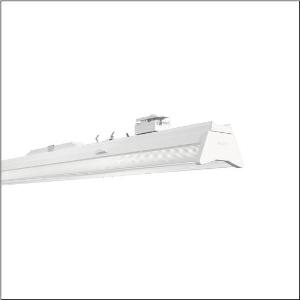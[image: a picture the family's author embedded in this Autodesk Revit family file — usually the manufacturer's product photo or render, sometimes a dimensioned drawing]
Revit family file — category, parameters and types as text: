
# Revit family: licross_r__21_performance_mo_51td16vn445g_3318
name_source: partatom
category: Lighting Fixtures
units: mm (PartAtom-declared; Revit-internal decimal feet)

## family parameters
Cut with Voids When Loaded = No
Host = Face
Light Source = No
Part Type = Normal
Room Calculation Point = No
Round Connector Dimension = Use Diameter
Shared = No

## types (1)
- --- (1 x LED, 4500 lm, 24.2 W, 4000K)
    Apparent Load = 24 VA
    CIE Flux Codes = 66 88 96 79 100
    Color Rendering = 80
    Color Temperature = 4000K
    Default Elevation = 1800 mm
    Description = Licross® 21 Performance MO, luminaire insert, of sheet steel, galvanised, coil coated, white, length: 1.500mm, width: 120mm, height: 123mm, LED rated luminous flux: 4.500lm, light colour: 840, SDCM (Standard Deviation of Colour Matching)MacAdam ≤ 2 SDCM (initial), control gear: DALI 2, CLO, with plug, 5-pole, with phase selection, mains connection: 220..240V, AC, 50/60Hz, start of lifetime: 24W, end of service life: 26W, internal wiring halogen-free, primary light control with lens, of plastic, primary optical cover: cover, of PMMA, light emission: direct/indirect distribution, primary light characteristic: symmetric, protection rating (complete): IP54, insulation class (complete): insulation class I (protective earthing), certification: CE, ENEC, VDE, UKCA, protection symbol: D if used in an environment with non-conductive dust loads with corresponding accessories, impact resistance: IK06, permissible ambient temperature for indoor applications: -25..+45°C, corresponds to IFS (International Featured Standards) requirements for safety and quality in the food industry, reducing of maximum allowable ambient temperature of 5°C with ceiling mounting, LABS conformity tested according to VDMA 24364:2018-05, packaging unit: 1 piece
    Height = 114 mm
    Lamp = 1 x LED
    Lamp Light Flux = 4500 lm
    Lamp Power = 24.2 W
    Lamp count = 1
    Length = 1500 mm
    Luminous efficacy = 186 lm/W
    Manufacturer = Siteco
    ModVariant = No
    Model = 51TD16VN445G
    Mounting Place = Ceiling
    Mounting Type = Pendant
    Number of Poles = 1
    OnlyDefault = Yes
    Power Factor = 1
    Product Name = Licross® 21 Performance MO
    Product group = luminaire insert | ceiling pendant
    ProductGroupID = 901
    Protection Class = Protection class I
    Protection Degree = IP 54
    RLX_Detail_Level = 1
    RLX_Emergency_Light_Flux = 0 lm
    RLX_Emergency_Type = 0
    RLX_Emergency_Type_DB = No
    RlxData = <blob elided: 33969 chars, md5=4ae669e8>
    Socket = socket
    Standby Power = 0 W
    System Light Flux = 4500 lm
    System Power = 24 W
    Type Comments = factory setting: luminous flux: 100 % | dim-lin: 254 | 160 mA
    Type Image = l_1256138.jpg
    URL = http://relux.com
    VarID = @adj_058881
    Voltage = 0 V
    Weight = 0.00 kg
    Width = 120 mm

## geometry (parser evidence)
native form markers: Blend x4, Sweep x11
no freeform markers — native parametric forms only
